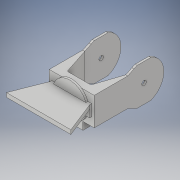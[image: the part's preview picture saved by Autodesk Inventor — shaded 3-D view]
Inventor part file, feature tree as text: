
AUTODESK INVENTOR PART (.ipt)
format: ipt  version: 2017 (Build 210142000, 142)  size: 209,408 bytes
history: native  units: in
note: dims shown in document units (in); Inventor stores cm internally (conversion verified against a paired STEP export)
features: extrude x7, sketch x7, plane x6, fillet x2, mirror x1
ambient origin geometry x8: Origin, YZ Plane, XZ Plane, XY Plane, X Axis, Y Axis, Z Axis, Center Point
bodies: Solid1 (feature_tree)
feature tree (23):
  extrude  "Extrusion1"  Depth=1.7323in
  plane  "Work Plane2"
  extrude  "Extrusion2"  Depth=1.7323in TaperAngle=0.0deg
  plane  "Work Plane4"
  extrude  "Extrusion3"  Depth=0.0787in
  fillet  "Fillet1"  Radius=0.0787in
  fillet  "Fillet2"  Radius=1.9094in
  sketch  "Sketch7"  dims[d25=0.2165in d29=0.0984in d30=0.0in]
  plane  "Work Plane6"
  extrude  "Extrusion4"  Depth=0.0984in TaperAngle=0.0deg
  mirror  "Mirror1"
  plane  "Work Plane7"
  extrude  "Extrusion5"  Depth=0.0984in TaperAngle=0.0deg
  plane  "Work Plane8"
  extrude  "Extrusion6"  Depth=1.4961in TaperAngle=0.0deg
  plane  "Work Plane10"
  extrude  "Extrusion7"  Depth=0.1969in
  sketch  "Sketch1"  dims[d0=2.1654in d1=1.7323in]
  sketch  "Sketch4"  dims[d2=1.6142in d3=0.0in d8=1.7323in d9=0.0in]
  sketch  "Sketch6"  dims[d17=1.7323in d18=0.0in d19=0.0787in d20=0.0787in d22=1.9094in]
  sketch  "Sketch10"  dims[d35=0.2165in d36=0.0984in d37=0.0in]
  sketch  "Sketch11"  dims[d39=0.1969in d40=1.4961in d41=0.0in]
  sketch  "Sketch13"  dims[d45=0.5906in d46=0.5906in d47=0.1969in d48=0.0in]
